# Revit family: Sirene Audiovisual SAVQE ILUMAC
name_source: partatom
category: Dispositivos de alarme de incêndio
units: mm (PartAtom-declared; Revit-internal decimal feet)

## family parameters
Com base no plano de trabalho = Não
Compartilhado = Não
Corte com vazios quando carregada = Não
Cota do conector redondo = Utilizar diâmetro
Manter orientação da anotação = Não
Número OmniClass = 23.75.00.00
Ponto de cálculo do ambiente = Não
Sempre na vertical = Sim
Tipo de parte = Normal
Título OmniClass = Climate Control (HVAC)

## types (4) — shared parameters
Consumo da fonte auxiliar ou V+ = 20mA em alarme
Dimensões (AxLxP) = 90x90x65mm
Endereços programáveis = 001 a 125 (por laço)
Endereços utilizados = 1 endereço
Fabricante = ILUMAC
Grau de proteção = IP20 (uso interno)
Material da caixa = Caixa plástica ABS na cor vermelho
Normas técnicas aplicáveis = NBR 17240 | ISO 7240-3 | ISO 7240-23
Peso = 200g
Secção máxima do cabo = 2,5mm²
Sinalização sonora = 103dB @ 1m – bitonal
Sinalização visual = 4 leds | Pisca na cor vermelha
Temperatura de operação = -5 à 55ºC
Tensão nominal = 24Vcc
Umidade relativa = 0 à 95% (sem condensação)
zero-valued in all types: Elevação padrão

## per-type parameters (varying)
| type | Adaptador ADAPT-Q (com/sem) | Consumo | Consumo do laço endereçável | Código do Produto | Descrição | Fixação | Modelo | Protocolo de comunicação | Tensão de operação |
| SAVQE-D – SOBREPOR | Não |  | 300uA em supervisão / 1.2mA em alarme | 0040261 | Sirene Audiovisual Endereçável Sirius SAVQE-D de sobrepor | Sobrepor c/ entrada superior/inferior para tubo 3/4“ | SAVQE-D – SOBREPOR | ALF-1000-2 (proprietário) | 18 à 30Vcc |
| SAVQE-D – EMBUTIR | Sim |  | 300uA em supervisão / 1.2mA em alarme | 0040262 | Sirene Audiovisual Endereçável Sirius SAVQE-D de embutir | Embutido c/ o uso do acessório ADAPT-Q | SAVQE-D – EMBUTIR | ALF-1000-2 (proprietário) | 18 à 30Vcc |
| SAVQE-G - EMBUTIR | Sim | 300uA em supervisão / 1.2mA em alarme |  | 007039 | Sirene Audiovisual Endereçável Cygnus SAVQE-G de embutir | Embutido c/ o uso do acessório ADAPT-Q | SAVQE-G – EMBUTIR | CYGNUS (proprietário) | 20 à 30Vcc |
| SAVQE-G - SOBREPOR | Sim | 300uA em supervisão / 1.2mA em alarme |  | 007038 | Sirene Audiovisual Endereçável Cygnus SAVQE-G de sobrepor | Sobrepor c/ entrada superior/inferior para tubo 3/4“ | SAVQE-G – SOBREPOR | CYGNUS (proprietário) | 20 à 30Vcc |
